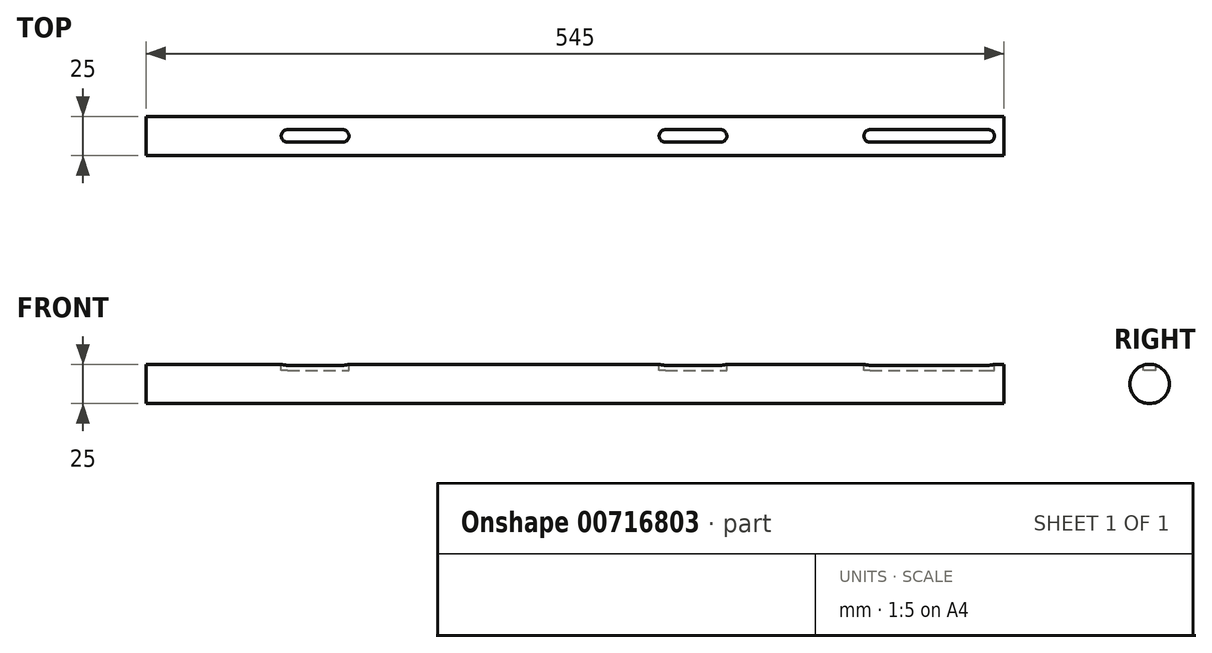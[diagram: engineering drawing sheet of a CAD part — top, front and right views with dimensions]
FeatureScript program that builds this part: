
annotation { "Feature Type Name" : "Feature", "Feature Type Description" : "" }
export const myFeature = defineFeature(function(context is Context, id is Id, definition is map)
    precondition{}
    {
        {
            var Q0;
            Q0=qCreatedBy(makeId("Right.planeOp"),FACE);
            var sketch = newSketch(context, id + "F0", { "sketchPlane" : qUnion([Q0])});
            skCircle(sketch, "E0", {"center": v(0, 0) * mm, "radius": 12.5 * mm});
            skSolve(sketch);
        }
        {
            var Q0;
            Q0=qCreatedBy(makeId("Top.planeOp"),FACE);
            cPlane(context, id + "F1", {"entities" : qUnion([Q0]), "cplaneType" : CPlaneType.OFFSET, "offset" : 12.5 * mm, "width" : 150 * mm, "height" : 150 * mm});
        }
        {
            var Q0;
            Q0=qSketchRegion(id+"F0",true);
            extrude(context, id + "F2", {"entities" : qUnion([Q0]), "endBound" : BoundingType.SYMMETRIC, "depth" : 545 * mm, "offsetDistance" : 25 * mm});
        }
        {
            var Q0;
            Q0=qCreatedBy(id+"F1.planeOp",FACE);
            var sketch = newSketch(context, id + "F3", { "sketchPlane" : qUnion([Q0])});
            skLineSegment(sketch, "E1", {"start": v(-182.5, 0) * mm, "end": v(-147.5, 0) * mm});
            skLineSegment(sketch, "E2", {"start": v(57.5, 0) * mm, "end": v(92.5, 0) * mm});
            skArc(sketch, "E3.0.startCap", {"start": v(-182.5, -4) * mm, "mid": v(-186.5, 0) * mm, "end": v(-182.5, 4) * mm});
            skArc(sketch, "E3.0.endCap", {"start": v(-147.5, 4) * mm, "mid": v(-143.5, 0) * mm, "end": v(-147.5, -4) * mm});
            skLineSegment(sketch, "E3.0.left", {"start": v(-182.5, 4) * mm, "end": v(-147.5, 4) * mm});
            skLineSegment(sketch, "E3.0.right", {"start": v(-182.5, -4) * mm, "end": v(-147.5, -4) * mm});
            skArc(sketch, "E3.1.startCap", {"start": v(57.5, -4) * mm, "mid": v(53.5, 0) * mm, "end": v(57.5, 4) * mm});
            skArc(sketch, "E3.1.endCap", {"start": v(92.5, 4) * mm, "mid": v(96.5, 0) * mm, "end": v(92.5, -4) * mm});
            skLineSegment(sketch, "E3.1.left", {"start": v(57.5, 4) * mm, "end": v(92.5, 4) * mm});
            skLineSegment(sketch, "E3.1.right", {"start": v(57.5, -4) * mm, "end": v(92.5, -4) * mm});
            skLineSegment(sketch, "E4", {"start": v(187.5, 0) * mm, "end": v(262.5, 0) * mm});
            skArc(sketch, "E5.1.startCap", {"start": v(187.5, -4) * mm, "mid": v(183.5, 0) * mm, "end": v(187.5, 4) * mm});
            skArc(sketch, "E5.1.endCap", {"start": v(262.5, 4) * mm, "mid": v(266.5, 0) * mm, "end": v(262.5, -4) * mm});
            skLineSegment(sketch, "E5.1.left", {"start": v(187.5, 4) * mm, "end": v(262.5, 4) * mm});
            skLineSegment(sketch, "E5.1.right", {"start": v(187.5, -4) * mm, "end": v(262.5, -4) * mm});
            skSolve(sketch);
        }
        {
            var Q0;
            Q0=qSketchRegion(id+"F3",true);
            extrude(context, id + "F4", {"entities" : qUnion([Q0]), "operationType" : NewBodyOperationType.REMOVE, "oppositeDirection" : true, "depth" : 4 * mm, "offsetDistance" : 25 * mm});
        }
    });
